# Revit family: Domotics-DomesticRanges-GEWISS-CHORUS_SIGNALLING-LAMP_EMERGENCY
name_source: partatom
category: Apparecchi elettrici
revit_build: Autodesk Revit 2016 (Build: 20161004_0715(x64)
units: mm (PartAtom-declared; Revit-internal decimal feet)

## family parameters
Condiviso = Sì
Host = Superficie
Mantenere orientamento annotazione = Sì
Punto di calcolo locali = Sì
Quota connettore circolare = Usa diametro
Taglio con vuoti quando caricato = Sì
Tipo di parte = Normale

## types (6) — shared parameters
Altezza_lampada = 45 mm  [stored 0.147638 ft]
Catalogue = DOMOTICS
Catalogue Range = CHORUS - DOMESTIC RANGE
Description. = Emergency lamp
Duration = 1H
Electrocod = 0781
IDF = 4be92484-c745-42b6-9079-ad998218b90c
IDT = f86042a5-691c-42dd-94bd-3c1ff62c387b
Immagine tipo = GW14666.jpg
Lamp = LED
Larghezza_lampada = 23 mm  [stored 0.0754593 ft]
Minimum autonomy = 1H
Offset_bidimensionale = 2 mm  [stored 0.00656168 ft]
Power supply batteries = Ni - Mh
Produttore = GEWISS S.p.A.
Prospetto di default = 1219 mm
SEO = Lamp
Supply voltage = 230 V ac - 50/60 Hz
Technical sheet = https://www.gewiss.com
Tipo_ = CHORUS LAMPADE EMERGENZA : GW14666 Lampada autonoma emergenza 230V ac 50/60Hz 2h titanio
Type of lamp = LED
URL = https://www.gewiss.com
Version file RFA = 19.0
finitura = GEWISS NERO

## per-type parameters (varying)
| type | Colour | Descrizione | EAN code | Modello | No. Chorus modules | No. Chorus modules: |
| GW10663 - Emergency lamp 2M 230V White | White | AUT. EMERGENCY LAMP, 2M 230V WHITE | 8011564840225 | GW10663 | 2 | 2 |
| GW14666 - Emergency lamp 230V ac 50/60Hz 2h Titanium | Titanium | AUT. EMERGENCY LAMP 230V AC 50/60Hz 2h T | 8011564268661 | GW14666 | 4 | 4 |
| GW12666 - Emergency lamp 230V ac 50/60Hz 2h Black | Black | AUT. EMERGENCY LAMP 230V AC 50/60Hz 2h B | 8011564267428 | GW12666 | 4 | 4 |
| GW10666 - Emergency lamp 230V ac 50/60Hz 2h White | White | AUT. EMERGENCY LAMP, 230VAC 50/60Hz 2h W | 8011564262935 | GW10666 | 4 | 4 |
| GW14663 - Emergency lamp 2M 230V Titanium | Titanium | AUT. EMERGENCY LAMP, 2M 230V TITANIUM | 8011564840249 | GW14663 | 2 | 2 |
| GW12663 - Emergency lamp 2M 230V Black | Black | AUT. EMERGENCY LAMP, 2M 230V BLACK | 8011564840232 | GW12663 | 2 | 2 |

note: [stored X ft] marks values corroborated as IEEE doubles in the binary element streams (Revit-internal decimal feet)

## geometry (parser evidence)
native form markers: Sweep x2
no freeform markers — native parametric forms only
